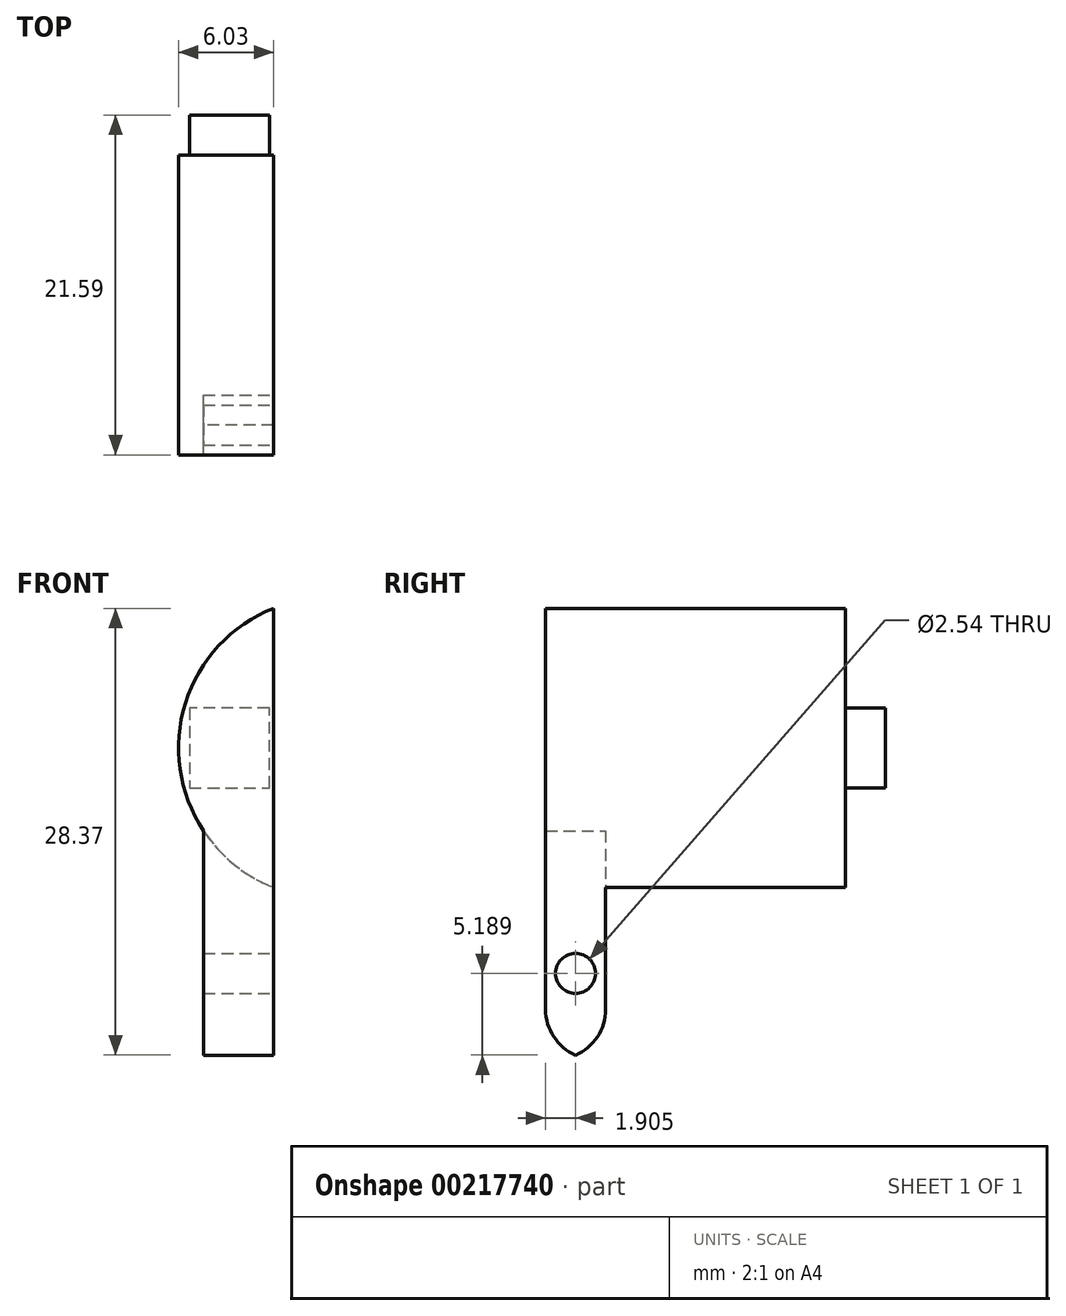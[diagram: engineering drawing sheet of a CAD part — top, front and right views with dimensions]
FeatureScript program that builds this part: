
annotation { "Feature Type Name" : "Feature", "Feature Type Description" : "" }
export const myFeature = defineFeature(function(context is Context, id is Id, definition is map)
    precondition{}
    {
        {
            var Q0;
            Q0=qCreatedBy(makeId("Front.planeOp"),FACE);
            var sketch = newSketch(context, id + "F0", { "sketchPlane" : qUnion([Q0])});
            skArc(sketch, "E0", {"start": v(-3.5, 8.86) * mm, "mid": v(-9.53, 0) * mm, "end": v(-3.5, -8.86) * mm});
            skLineSegment(sketch, "E1", {"start": v(-3.5, 0) * mm, "end": v(-3.5, 8.86) * mm});
            skLineSegment(sketch, "E2", {"start": v(-3.5, 0) * mm, "end": v(-3.5, -8.86) * mm});
            skPoint(sketch, "E3.orphan", {"position": v(0, -9.53) * mm});
            skSolve(sketch);
        }
        {
            var Q0;
            Q0 = qSketchRegion(id + "F0", true);
            extrude(context, id + "F1", {"entities" : qUnion([Q0]), "depth" : 19.05 * mm});
        }
        {
            var Q0;
            Q0=makeQuery(id+"F1.opExtrude","CAP_FACE",FACE,{"disambiguationData":[OSD([sQuery(id+"F0.wireOp",EDGE,"E0"),sQuery(id+"F0.wireOp",EDGE,"E1"),sQuery(id+"F0.wireOp",EDGE,"E2")])],"isStart":true});
            var sketch = newSketch(context, id + "F2", { "sketchPlane" : qUnion([Q0])});
            skLineSegment(sketch, "E4", {"start": v(3.75, 0) * mm, "end": v(3.75, 2.54) * mm});
            skLineSegment(sketch, "E5", {"start": v(3.75, 2.54) * mm, "end": v(8.83, 2.54) * mm});
            skLineSegment(sketch, "E6", {"start": v(8.83, 2.54) * mm, "end": v(8.83, -2.54) * mm});
            skLineSegment(sketch, "E7", {"start": v(8.83, -2.54) * mm, "end": v(3.75, -2.54) * mm});
            skLineSegment(sketch, "E8", {"start": v(3.75, -2.54) * mm, "end": v(3.75, 0) * mm});
            skSolve(sketch);
        }
        {
            var Q0;
            Q0 = qSketchRegion(id + "F2", true);
            extrude(context, id + "F3", {"entities" : qUnion([Q0]), "operationType" : NewBodyOperationType.ADD, "depth" : 2.54 * mm});
        }
        {
            var Q0;
            Q0=makeQuery(id+"F1.opExtrude","SWEPT_FACE",FACE,{"disambiguationData":[OSD([sQuery(id+"F0.wireOp",EDGE,"E1"),sQuery(id+"F0.wireOp",EDGE,"E2")])]});
            var sketch = newSketch(context, id + "F4", { "sketchPlane" : qUnion([Q0])});
            skLineSegment(sketch, "E9.left", {"start": v(-19.05, -8.86) * mm, "end": v(-19.05, -19.78) * mm});
            skLineSegment(sketch, "E9.right", {"start": v(-15.24, -8.86) * mm, "end": v(-15.24, -19.78) * mm});
            skLineSegment(sketch, "E10.top", {"start": v(-19.05, -2.04) * mm, "end": v(-15.24, -2.04) * mm});
            skLineSegment(sketch, "E10.left", {"start": v(-19.05, -8.86) * mm, "end": v(-19.05, -2.04) * mm});
            skLineSegment(sketch, "E10.right", {"start": v(-15.24, -8.86) * mm, "end": v(-15.24, -2.04) * mm});
            skLineSegment(sketch, "E11", {"start": v(-19.05, -19.78) * mm, "end": v(-15.24, -19.78) * mm});
            skSolve(sketch);
        }
        {
            var Q0;
            Q0 = qSketchRegion(id + "F4", true);
            extrude(context, id + "F5", {"entities" : qUnion([Q0]), "operationType" : NewBodyOperationType.ADD, "oppositeDirection" : true, "depth" : 4.44 * mm});
        }
        {
            var Q0;
            Q0=makeQuery(id+"F5.opExtrude","CAP_FACE",FACE,{"disambiguationData":[OSD([sQuery(id+"F4.wireOp",EDGE,"E9.top"),sQuery(id+"F4.wireOp",EDGE,"E9.left"),sQuery(id+"F4.wireOp",EDGE,"E9.right"),sQuery(id+"F4.wireOp",EDGE,"E10.top"),sQuery(id+"F4.wireOp",EDGE,"E10.left"),sQuery(id+"F4.wireOp",EDGE,"E10.right")])],"isStart":true});
            var sketch = newSketch(context, id + "F6", { "sketchPlane" : qUnion([Q0])});
            skCircle(sketch, "E12", {"center": v(-17.14, -14.32) * mm, "radius": 1.27 * mm});
            skPoint(sketch, "E12.centerSnap0", {"position": v(-15.24, -14.32) * mm});
            skSolve(sketch);
        }
        {
            var Q0;
            Q0 = qSketchRegion(id + "F6", true);
            extrude(context, id + "F7", {"entities" : qUnion([Q0]), "operationType" : NewBodyOperationType.REMOVE, "oppositeDirection" : true, "depth" : 25.4 * mm});
        }
        {
            var Q0;
            Q0=makeQuery(id+"F5.opExtrude","SWEPT_EDGE",EDGE,{"disambiguationData":[OSD([sQuery(id+"F4.wireOp",EDGE,"E9.right"),sQuery(id+"F4.wireOp",EDGE,"E11")])]});
            var Q1;
            Q1=makeQuery(id+"F5.opExtrude","SWEPT_EDGE",EDGE,{"disambiguationData":[OSD([sQuery(id+"F4.wireOp",EDGE,"E9.left"),sQuery(id+"F4.wireOp",EDGE,"E11")])]});
            fillet(context, id + "F8", {"entities" : qUnion([Q0, Q1]), "radius" : 3.17 * mm, "tangentPropagation" : true, "allowEdgeOverflow" : false});
        }
    });
